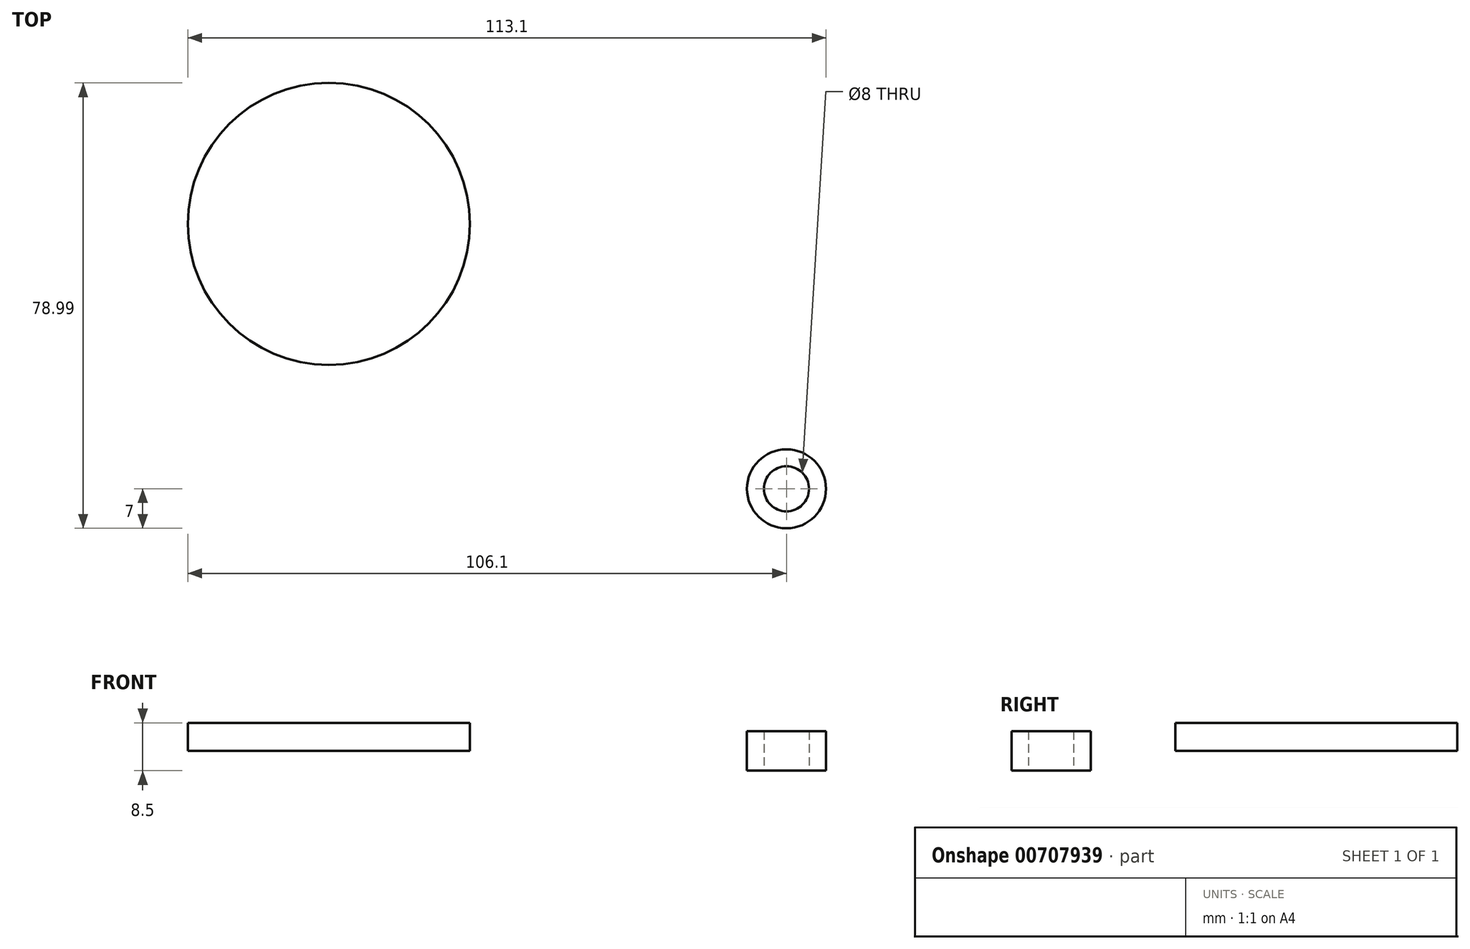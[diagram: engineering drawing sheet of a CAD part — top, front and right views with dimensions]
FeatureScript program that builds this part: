
annotation { "Feature Type Name" : "Feature", "Feature Type Description" : "" }
export const myFeature = defineFeature(function(context is Context, id is Id, definition is map)
    precondition{}
    {
        {
            var Q0;
            Q0=qCreatedBy(makeId("Top.planeOp"),FACE);
            var sketch = newSketch(context, id + "F0", { "sketchPlane" : qUnion([Q0])});
            skCircle(sketch, "E0", {"center": v(0, 0) * mm, "radius": 4 * mm});
            skCircle(sketch, "E1", {"center": v(0, 0) * mm, "radius": 7 * mm});
            skSolve(sketch);
        }
        {
            var Q0;
            Q0=makeQuery(id+"F0.imprint","IMPRINT",FACE,{"disambiguationData":[TD([[makeQuery(id+"F0.imprint","IMPRINT",EDGE,{"derivedFrom":sQuery(id+"F0.wireOp",EDGE,"E0")}),-1.0]])]});
            extrude(context, id + "F1", {"entities" : qUnion([Q0]), "endBound" : BoundingType.SYMMETRIC, "depth" : 7 * mm, "offsetDistance" : 25 * mm});
        }
        {
            var Q0;
            Q0=qCreatedBy(makeId("Top.planeOp"),FACE);
            var sketch = newSketch(context, id + "F2", { "sketchPlane" : qUnion([Q0])});
            skCircle(sketch, "E2", {"center": v(-81.1, 47) * mm, "radius": 25 * mm});
            skSolve(sketch);
        }
        {
            var Q0;
            Q0 = qSketchRegion(id + "F2", true);
            extrude(context, id + "F3", {"entities" : qUnion([Q0]), "depth" : 5 * mm, "offsetDistance" : 25 * mm});
        }
    });
